# Revit family: 63_UN_FreeStanding_KFA LED_Norton
name_source: partatom
category: Lighting Fixtures
units: mm (PartAtom-declared; Revit-internal decimal feet)

## family parameters
Always vertical = Yes
Cut with Voids When Loaded = Yes
Light Source = No
OmniClass Number = 23.80.70.11.14.11
OmniClass Title = Downlights
Part Type = Normal
Room Calculation Point = Yes
Round Connector Dimension = Use Diameter
Shared = No
Work Plane-Based = No

## types (11) — shared parameters
Assembly Code = 63.0
Description = IP66 / IK10
IfcExportAs = IfcLightFixtureType
IfcExportType = USERDEFINED
Lamp = LED
Manufacturer = Norton
Model = KFA LED
URL = https://www.norton.nl
Voltage = 230 V

## per-type parameters (varying)
| type | Apparent Load | Calc_Symbol_Length | Calc_Symbol_Width | Housing_Material | L454 | L474 | L544 | Light Source | Luminous Flux (lm) | Wattage Comments | Weight |
| L454 - 2000lm - Anthracite | 16 VA | 327 mm | 234 mm  [stored 0.767717 ft] | Anthracite | Yes | No | No | KFA L454 Geometry WM : 2000lm | 2000 lm | 16W | 4kg |
| L454 - 2000lm - Gray | 16 VA | 327 mm | 234 mm  [stored 0.767717 ft] | Gray | Yes | No | No | KFA L454 Geometry WM : 2000lm | 2000 lm | 16W | 4kg |
| L454 - 2700lm - Anthracite | 35 VA | 327 mm | 234 mm  [stored 0.767717 ft] | Anthracite | Yes | No | No | KFA L454 Geometry WM : 2700lm | 2000 lm | 35W | 4kg |
| L454 - 4000lm - Anthracite | 35 VA | 327 mm | 234 mm  [stored 0.767717 ft] | Anthracite | Yes | No | No | KFA L454 Geometry WM : 4000lm | 4000 lm | 35W | 4kg |
| L454 - 4000lm - Gray | 35 VA | 327 mm | 234 mm  [stored 0.767717 ft] | Gray | Yes | No | No | KFA L454 Geometry WM : 4000lm | 4000 lm | 35W | 4kg |
| L454 - 5500lm - Anthracite | 50 VA | 327 mm | 234 mm  [stored 0.767717 ft] | Anthracite | Yes | No | No | KFA L454 Geometry WM : 5500lm | 5500 lm | 50W | 4kg |
| L454 - 5500lm - Gray | 50 VA | 327 mm | 234 mm  [stored 0.767717 ft] | Gray | Yes | No | No | KFA L454 Geometry WM : 5500lm | 5500 lm | 50W | 4kg |
| L474 - 11800lm - Anthracite | 110 VA | 345 mm  [stored 1.13189 ft] | 354 mm  [stored 1.16142 ft] | Anthracite | No | Yes | No | KFA L474 Geometry WM : 11800lm | 5500 lm | 110W | 5,9kg |
| L474 - 11800lm - Gray | 110 VA | 415 mm | 354 mm  [stored 1.16142 ft] | Gray | No | Yes | No | KFA L474 Geometry WM : 11800lm | 5500 lm | 110W | 5,9kg |
| L544 - 17000lm - Anthracite | 110 VA | 415 mm | 354 mm  [stored 1.16142 ft] | Anthracite | No | No | Yes | KFA L544 Geometry WM : 17000lm | 5500 lm | 110W | 6,5kg |
| L544 - 17000lm - Gray | 110 VA | 415 mm | 354 mm  [stored 1.16142 ft] | Gray | No | No | Yes | KFA L544 Geometry WM : 17000lm | 5500 lm | 110W | 6,5kg |

note: [stored X ft] marks values corroborated as IEEE doubles in the binary element streams (Revit-internal decimal feet)

## geometry (parser evidence)
native form markers: Sweep x25
no freeform markers — native parametric forms only
